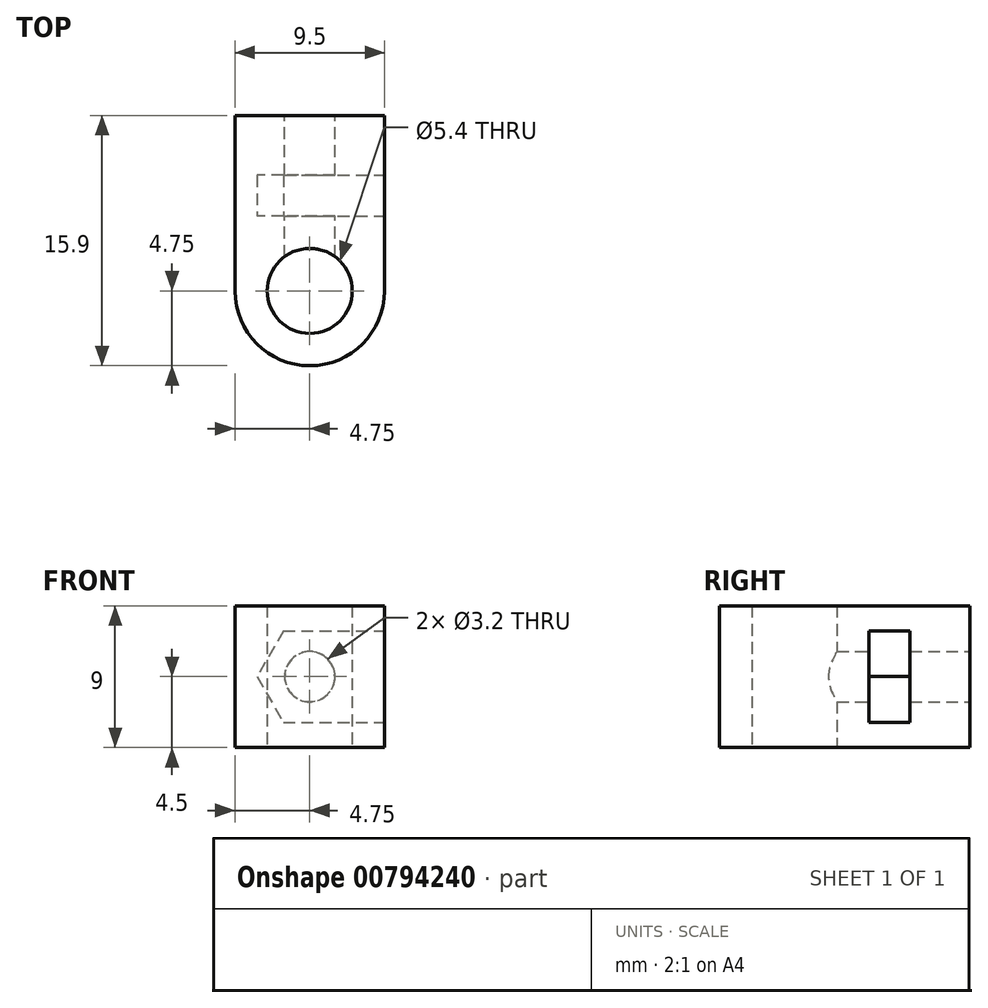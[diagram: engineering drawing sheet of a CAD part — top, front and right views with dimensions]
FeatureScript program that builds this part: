
annotation { "Feature Type Name" : "Feature", "Feature Type Description" : "" }
export const myFeature = defineFeature(function(context is Context, id is Id, definition is map)
    precondition{}
    {
        {
            var Q0;
            Q0=qCreatedBy(makeId("Top.planeOp"),FACE);
            var sketch = newSketch(context, id + "F0", { "sketchPlane" : qUnion([Q0])});
            skCircle(sketch, "E0", {"center": v(0, 0) * mm, "radius": 2.7 * mm});
            skCircle(sketch, "E1", {"center": v(0, 0) * mm, "radius": 4.75 * mm});
            skLineSegment(sketch, "E2", {"start": v(-4.75, 0) * mm, "end": v(-4.75, 4.75) * mm});
            skLineSegment(sketch, "E3", {"start": v(4.75, 0) * mm, "end": v(4.75, 4.75) * mm});
            skLineSegment(sketch, "E4", {"start": v(0, 4.75) * mm, "end": v(-4.75, 4.75) * mm});
            skLineSegment(sketch, "E5", {"start": v(-4.75, 4.75) * mm, "end": v(4.75, 4.75) * mm});
            skSolve(sketch);
        }
        {
            var Q0;
            {var subQ0=sQuery(id+"F0.wireOp",EDGE,"E3");Q0=makeQuery(id+"F0.imprint","IMPRINT",FACE,{"disambiguationData":[TD([[makeQuery(id+"F0.imprint","IMPRINT",EDGE,{"derivedFrom":subQ0}),1.0]])]});}
            var Q1;
            {var subQ0=sQuery(id+"F0.wireOp",EDGE,"E2");Q1=makeQuery(id+"F0.imprint","IMPRINT",FACE,{"disambiguationData":[TD([[makeQuery(id+"F0.imprint","IMPRINT",EDGE,{"derivedFrom":subQ0}),-1.0]])]});}
            var Q2;
            Q2=makeQuery(id+"F0.imprint","IMPRINT",FACE,{"disambiguationData":[TD([[makeQuery(id+"F0.imprint","IMPRINT",EDGE,{"derivedFrom":sQuery(id+"F0.wireOp",EDGE,"E0")}),-1.0]])]});
            extrude(context, id + "F1", {"entities" : qUnion([Q0, Q1, Q2]), "depth" : 9 * mm, "offsetDistance" : 25.4 * mm});
        }
        {
            var Q0;
            Q0=makeQuery(id+"F1.opExtrude","SWEPT_FACE",FACE,{"disambiguationData":[OSD([sQuery(id+"F0.wireOp",EDGE,"E5")])]});
            var sketch = newSketch(context, id + "F2", { "sketchPlane" : qUnion([Q0])});
            skLineSegment(sketch, "E6", {"start": v(-4.75, 9) * mm, "end": v(4.75, 0) * mm, "construction": true});
            skLineSegment(sketch, "E7", {"start": v(-4.75, 0) * mm, "end": v(4.75, 9) * mm, "construction": true});
            skCircle(sketch, "E8.cCircle", {"center": v(0, 4.5) * mm, "radius": 2.9 * mm, "construction": true});
            skLineSegment(sketch, "E8.0", {"start": v(-1.67, 7.4) * mm, "end": v(1.67, 7.4) * mm});
            skLineSegment(sketch, "E8.1", {"start": v(1.67, 7.4) * mm, "end": v(3.35, 4.5) * mm});
            skLineSegment(sketch, "E8.2", {"start": v(3.35, 4.5) * mm, "end": v(1.67, 1.6) * mm});
            skLineSegment(sketch, "E8.3", {"start": v(1.67, 1.6) * mm, "end": v(-1.67, 1.6) * mm});
            skLineSegment(sketch, "E8.4", {"start": v(-1.67, 1.6) * mm, "end": v(-3.35, 4.5) * mm});
            skLineSegment(sketch, "E8.5", {"start": v(-3.35, 4.5) * mm, "end": v(-1.67, 7.4) * mm});
            skPoint(sketch, "E8.0.midPoint", {"position": v(0, 7.4) * mm});
            skLineSegment(sketch, "E9", {"start": v(-1.67, 7.4) * mm, "end": v(-4.75, 7.4) * mm});
            skLineSegment(sketch, "E10", {"start": v(1.67, 1.6) * mm, "end": v(-4.75, 1.6) * mm});
            skSolve(sketch);
        }
        {
            var Q0;
            Q0=makeQuery(id+"F2.imprint","IMPRINT",FACE,{"disambiguationData":[TD([[makeQuery(id+"F2.imprint","IMPRINT",EDGE,{"derivedFrom":sQuery(id+"F2.wireOp",EDGE,"E8.0")}),1.0]])]});
            extrude(context, id + "F3", {"entities" : qUnion([Q0]), "operationType" : NewBodyOperationType.ADD, "depth" : 2.6 * mm, "offsetDistance" : 25.4 * mm});
        }
        {
            var Q0;
            Q0=makeQuery(id+"F3.opExtrude","CAP_FACE",FACE,{"disambiguationData":[OSD([sQuery(id+"F0.wireOp",EDGE,"E2"),sQuery(id+"F0.wireOp",EDGE,"E3"),sQuery(id+"F0.wireOp",EDGE,"E5"),sQuery(id+"F2.wireOp",EDGE,"E8.0"),sQuery(id+"F2.wireOp",EDGE,"E8.1"),sQuery(id+"F2.wireOp",EDGE,"E8.2"),sQuery(id+"F2.wireOp",EDGE,"E9"),sQuery(id+"F2.wireOp",EDGE,"E10")])],"isStart":false});
            var sketch = newSketch(context, id + "F4", { "sketchPlane" : qUnion([Q0])});
            skLineSegment(sketch, "E11.bottom", {"start": v(-4.75, 9) * mm, "end": v(4.75, 9) * mm});
            skLineSegment(sketch, "E11.top", {"start": v(-4.75, 0) * mm, "end": v(4.75, 0) * mm});
            skLineSegment(sketch, "E11.left", {"start": v(-4.75, 9) * mm, "end": v(-4.75, 0) * mm});
            skLineSegment(sketch, "E11.right", {"start": v(4.75, 9) * mm, "end": v(4.75, 0) * mm});
            skSolve(sketch);
        }
        {
            var Q0;
            Q0 = qSketchRegion(id + "F4", true);
            extrude(context, id + "F5", {"entities" : qUnion([Q0]), "operationType" : NewBodyOperationType.ADD, "depth" : 3.8 * mm, "offsetDistance" : 25.4 * mm});
        }
        {
            var Q0;
            Q0=makeQuery(id+"F5.opExtrude","CAP_FACE",FACE,{"disambiguationData":[OSD([sQuery(id+"F4.wireOp",EDGE,"E11.bottom"),sQuery(id+"F4.wireOp",EDGE,"E11.top"),sQuery(id+"F4.wireOp",EDGE,"E11.left"),sQuery(id+"F4.wireOp",EDGE,"E11.right")])],"isStart":false});
            var sketch = newSketch(context, id + "F6", { "sketchPlane" : qUnion([Q0])});
            skLineSegment(sketch, "E12", {"start": v(-4.75, 0) * mm, "end": v(4.75, 9) * mm, "construction": true});
            skLineSegment(sketch, "E13", {"start": v(-4.75, 9) * mm, "end": v(4.75, 0) * mm, "construction": true});
            skCircle(sketch, "E14", {"center": v(0, 4.5) * mm, "radius": 1.6 * mm});
            skSolve(sketch);
        }
        {
            var Q0;
            Q0=makeQuery(id+"F6.imprint","IMPRINT",FACE,{"disambiguationData":[TD([[makeQuery(id+"F6.imprint","IMPRINT",EDGE,{"derivedFrom":sQuery(id+"F6.wireOp",EDGE,"E14")}),1.0]])]});
            var Q1;
            Q1=sQuery(id+"F6.wireOp",EDGE,"E14");
            extrude(context, id + "F7", {"entities" : qUnion([Q0]), "operationType" : NewBodyOperationType.REMOVE, "surfaceEntities" : qUnion([Q1]), "oppositeDirection" : true, "depth" : 9 * mm, "offsetDistance" : 25.4 * mm});
        }
    });
